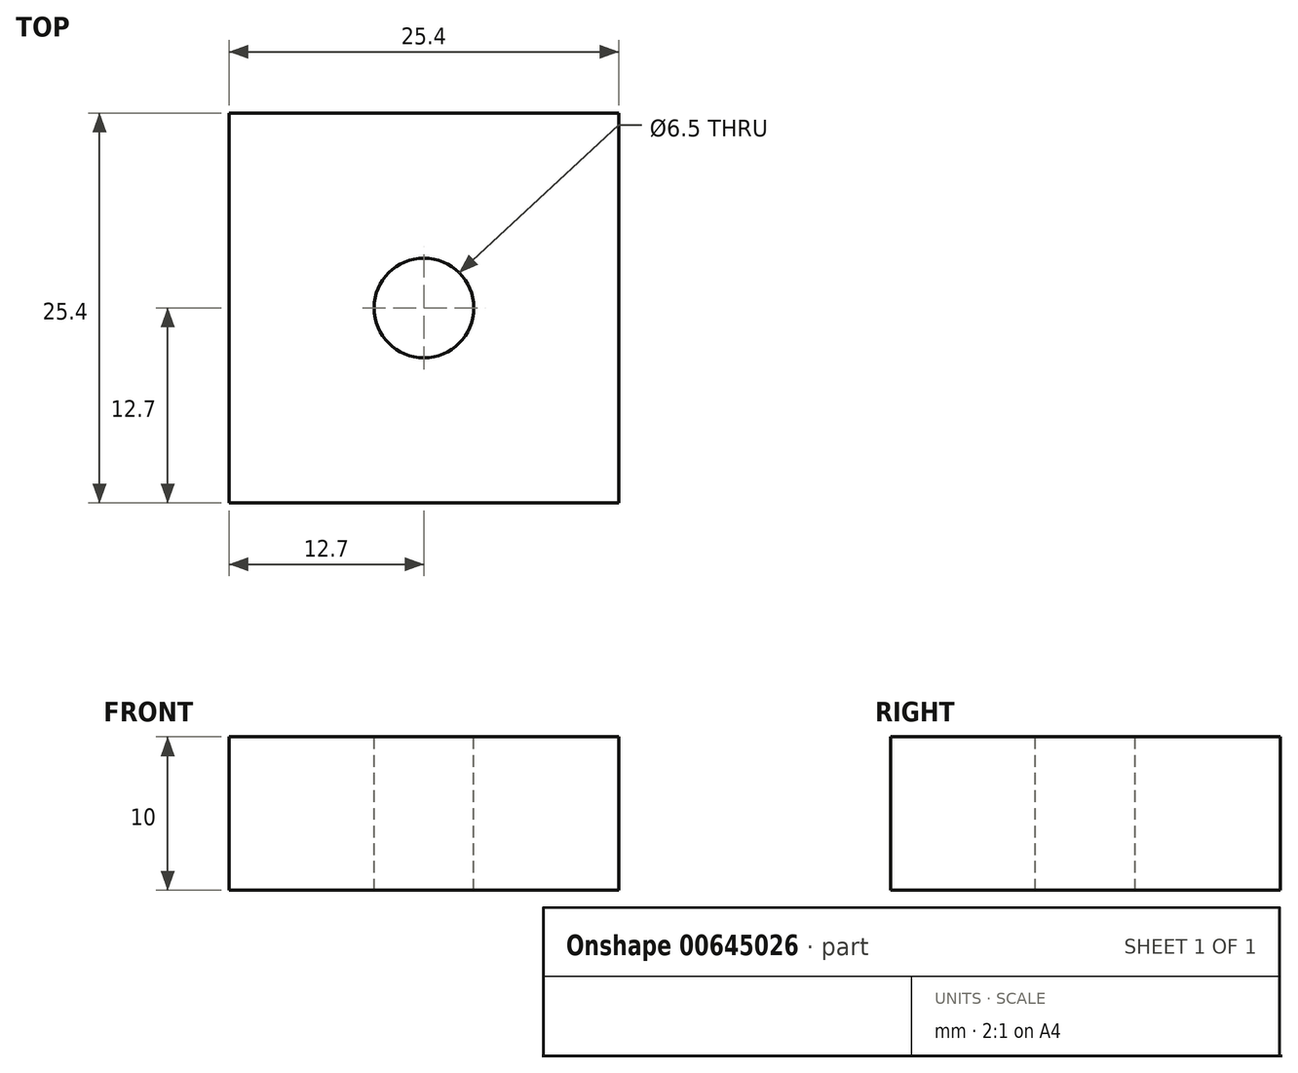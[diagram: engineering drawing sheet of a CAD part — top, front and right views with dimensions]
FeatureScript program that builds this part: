
annotation { "Feature Type Name" : "Feature", "Feature Type Description" : "" }
export const myFeature = defineFeature(function(context is Context, id is Id, definition is map)
    precondition{}
    {
        {
            var Q0;
            Q0=qCreatedBy(makeId("Top.planeOp"),FACE);
            var sketch = newSketch(context, id + "F0", { "sketchPlane" : qUnion([Q0])});
            skLineSegment(sketch, "E0.bottom", {"start": v(12.7, -12.7) * mm, "end": v(-12.7, -12.7) * mm});
            skLineSegment(sketch, "E0.top", {"start": v(12.7, 12.7) * mm, "end": v(-12.7, 12.7) * mm});
            skLineSegment(sketch, "E0.left", {"start": v(12.7, -12.7) * mm, "end": v(12.7, 12.7) * mm});
            skLineSegment(sketch, "E0.right", {"start": v(-12.7, -12.7) * mm, "end": v(-12.7, 12.7) * mm});
            skPoint(sketch, "E0.middle", {"position": v(0, 0) * mm});
            skSolve(sketch);
        }
        {
            var Q0;
            Q0 = qSketchRegion(id + "F0", true);
            extrude(context, id + "F1", {"entities" : qUnion([Q0]), "depth" : 10 * mm, "offsetDistance" : 25.4 * mm});
        }
        {
            var Q0;
            Q0=makeQuery(id+"F1.opExtrude","CAP_FACE",FACE,{"disambiguationData":[OSD([sQuery(id+"F0.wireOp",EDGE,"E0.bottom"),sQuery(id+"F0.wireOp",EDGE,"E0.top"),sQuery(id+"F0.wireOp",EDGE,"E0.left"),sQuery(id+"F0.wireOp",EDGE,"E0.right")])],"isStart":false});
            var sketch = newSketch(context, id + "F2", { "sketchPlane" : qUnion([Q0])});
            skCircle(sketch, "E1", {"center": v(0, 0) * mm, "radius": 3.25 * mm});
            skSolve(sketch);
        }
        {
            var Q0;
            Q0 = qSketchRegion(id + "F2", true);
            extrude(context, id + "F3", {"entities" : qUnion([Q0]), "operationType" : NewBodyOperationType.REMOVE, "endBound" : BoundingType.UP_TO_NEXT, "oppositeDirection" : true, "depth" : 25.4 * mm, "offsetDistance" : 25.4 * mm});
        }
    });
